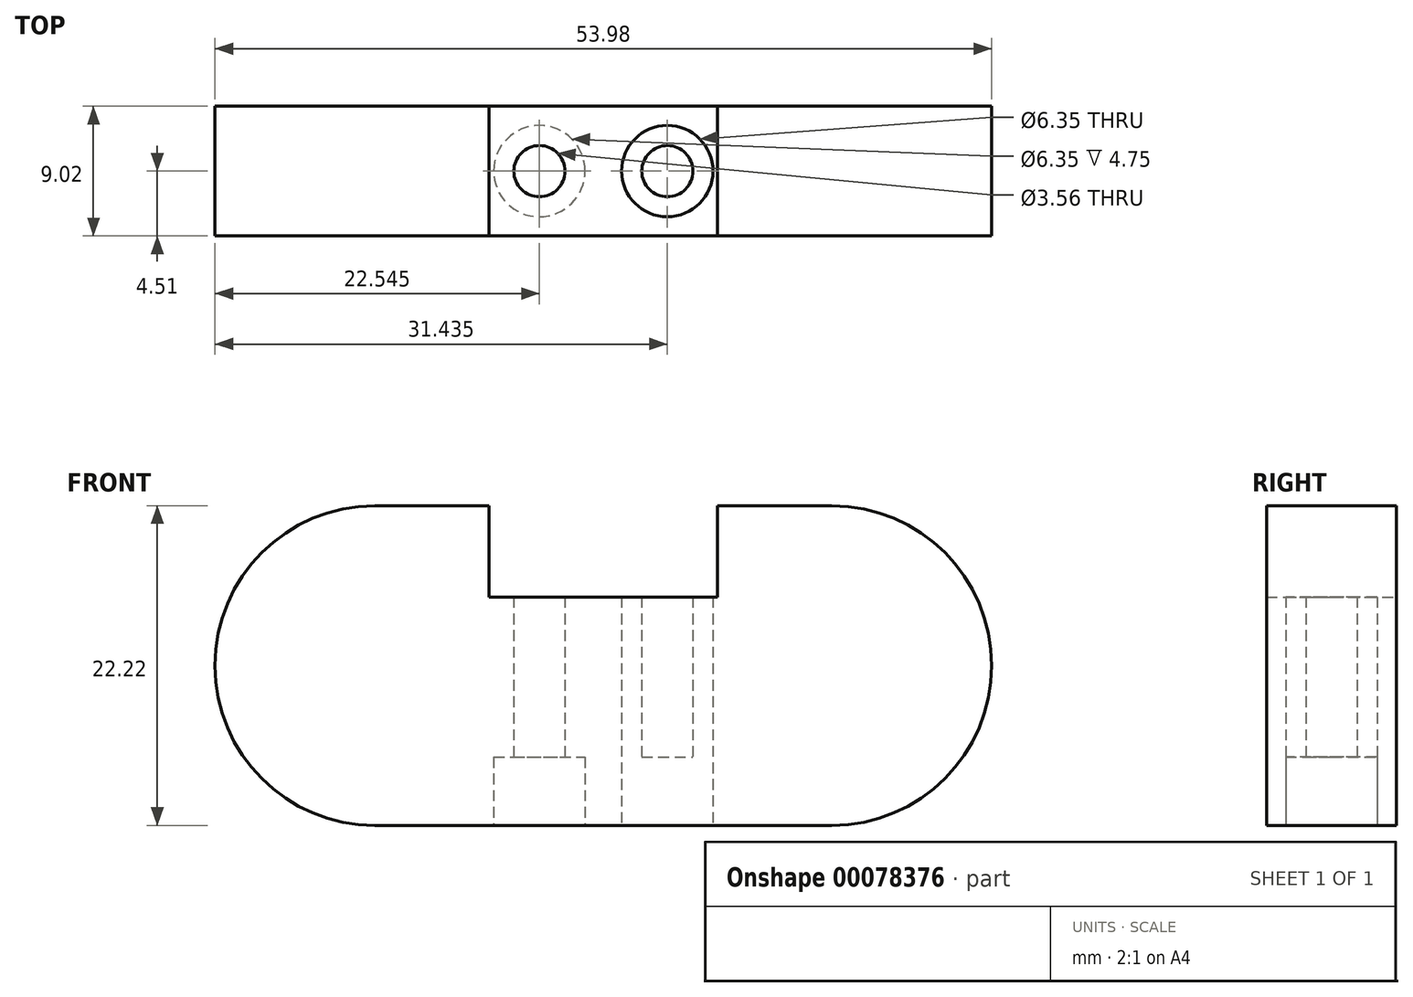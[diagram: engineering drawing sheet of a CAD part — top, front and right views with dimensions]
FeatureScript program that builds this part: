
annotation { "Feature Type Name" : "Feature", "Feature Type Description" : "" }
export const myFeature = defineFeature(function(context is Context, id is Id, definition is map)
    precondition{}
    {
        {
            var Q0;
            Q0=qCreatedBy(makeId("Front.planeOp"),FACE);
            var sketch = newSketch(context, id + "F0", { "sketchPlane" : qUnion([Q0])});
            skArc(sketch, "E0", {"start": v(-15.88, 11.11) * mm, "mid": v(-23.73, 7.86) * mm, "end": v(-26.99, 0) * mm});
            skLineSegment(sketch, "E1", {"start": v(-15.88, 11.11) * mm, "end": v(-7.94, 11.11) * mm});
            skLineSegment(sketch, "E2.MirrorCS", {"start": v(15.88, 11.11) * mm, "end": v(7.94, 11.11) * mm});
            skArc(sketch, "E3.MirrorCS", {"start": v(15.88, 11.11) * mm, "mid": v(23.73, 7.86) * mm, "end": v(26.99, 0) * mm});
            skArc(sketch, "E4.MirrorCS", {"start": v(-15.88, -11.11) * mm, "mid": v(-23.73, -7.86) * mm, "end": v(-26.99, 0) * mm});
            skLineSegment(sketch, "E5.MirrorCS", {"start": v(-15.88, -11.11) * mm, "end": v(0, -11.11) * mm});
            skLineSegment(sketch, "E6.MirrorCS", {"start": v(15.88, -11.11) * mm, "end": v(0, -11.11) * mm});
            skArc(sketch, "E7.MirrorCS", {"start": v(15.88, -11.11) * mm, "mid": v(23.73, -7.86) * mm, "end": v(26.99, 0) * mm});
            skLineSegment(sketch, "E8", {"start": v(-7.94, 11.11) * mm, "end": v(-7.94, 4.76) * mm});
            skLineSegment(sketch, "E9", {"start": v(-7.94, 4.76) * mm, "end": v(0, 4.76) * mm});
            skLineSegment(sketch, "E10.MirrorCS", {"start": v(7.94, 11.11) * mm, "end": v(7.94, 4.76) * mm});
            skLineSegment(sketch, "E11.MirrorCS", {"start": v(7.94, 4.76) * mm, "end": v(0, 4.76) * mm});
            skPoint(sketch, "E12.orphan", {"position": v(0, 11.11) * mm});
            skSolve(sketch);
        }
        {
            var Q0;
            Q0 = qSketchRegion(id + "F0", true);
            extrude(context, id + "F1", {"entities" : qUnion([Q0]), "endBound" : BoundingType.SYMMETRIC, "depth" : 9.02 * mm});
        }
        {
            var Q0;
            Q0=makeQuery(id+"F1.opExtrude","SWEPT_FACE",FACE,{"disambiguationData":[OSD([sQuery(id+"F0.wireOp",EDGE,"E5.MirrorCS"),sQuery(id+"F0.wireOp",EDGE,"E6.MirrorCS")])]});
            var sketch = newSketch(context, id + "F2", { "sketchPlane" : qUnion([Q0])});
            skLineSegment(sketch, "E13", {"start": v(0, 0) * mm, "end": v(-4.45, 0) * mm, "construction": true});
            skCircle(sketch, "E14", {"center": v(-4.45, 0) * mm, "radius": 3.18 * mm});
            skCircle(sketch, "E15.MirrorC", {"center": v(4.45, 0) * mm, "radius": 3.18 * mm});
            skSolve(sketch);
        }
        {
            var Q0;
            Q0 = qSketchRegion(id + "F2", true);
            extrude(context, id + "F3", {"entities" : qUnion([Q0]), "operationType" : NewBodyOperationType.REMOVE, "oppositeDirection" : true, "depth" : 4.75 * mm});
        }
        {
            var Q0;
            Q0=makeQuery(id+"F1.opExtrude","SWEPT_FACE",FACE,{"disambiguationData":[OSD([sQuery(id+"F0.wireOp",EDGE,"E5.MirrorCS"),sQuery(id+"F0.wireOp",EDGE,"E6.MirrorCS")])]});
            var sketch = newSketch(context, id + "F4", { "sketchPlane" : qUnion([Q0])});
            skLineSegment(sketch, "E16", {"start": v(0, 0) * mm, "end": v(-4.45, 0) * mm, "construction": true});
            skCircle(sketch, "E17", {"center": v(-4.45, 0) * mm, "radius": 1.78 * mm});
            skCircle(sketch, "E18.MirrorC", {"center": v(4.45, 0) * mm, "radius": 1.78 * mm});
            skSolve(sketch);
        }
        {
            var Q0;
            Q0=makeQuery(id+"F4.imprint","IMPRINT",FACE,{"disambiguationData":[TD([[makeQuery(id+"F4.imprint","IMPRINT",EDGE,{"derivedFrom":sQuery(id+"F4.wireOp",EDGE,"E17")}),1.0]])]});
            var Q1;
            Q1=makeQuery(id+"F4.imprint","IMPRINT",FACE,{"disambiguationData":[TD([[makeQuery(id+"F4.imprint","IMPRINT",EDGE,{"derivedFrom":sQuery(id+"F4.wireOp",EDGE,"E18.MirrorC")}),-1.0]])]});
            extrude(context, id + "F5", {"entities" : qUnion([Q0, Q1]), "operationType" : NewBodyOperationType.REMOVE, "oppositeDirection" : true, "depth" : 25.4 * mm});
        }
    });
